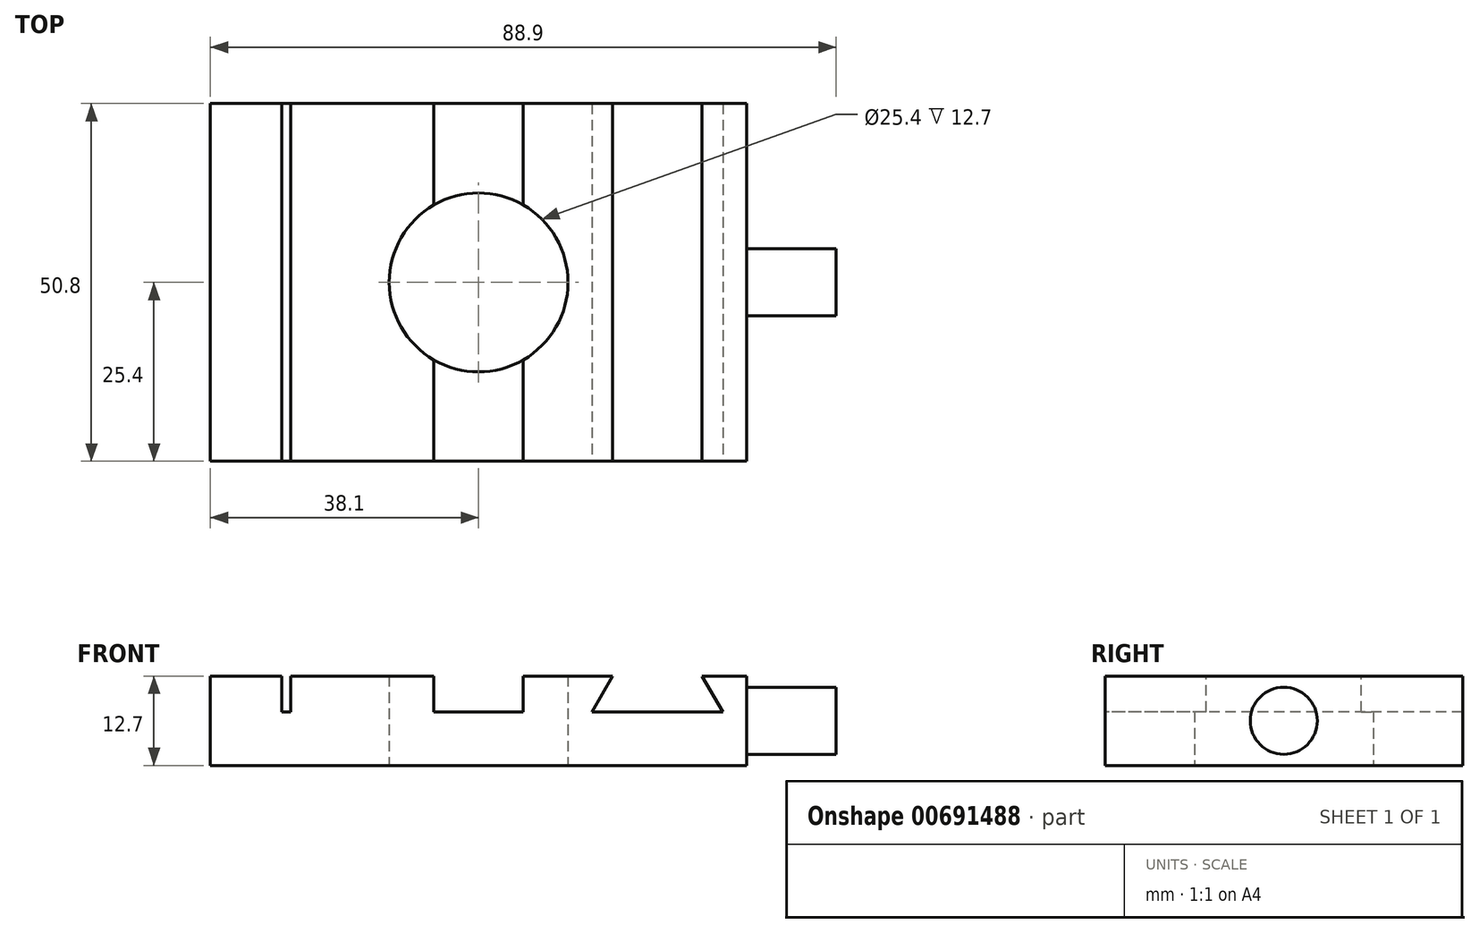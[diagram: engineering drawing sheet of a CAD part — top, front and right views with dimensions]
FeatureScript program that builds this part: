
annotation { "Feature Type Name" : "Feature", "Feature Type Description" : "" }
export const myFeature = defineFeature(function(context is Context, id is Id, definition is map)
    precondition{}
    {
        {
            var Q0;
            Q0=qCreatedBy(makeId("Top.planeOp"),FACE);
            var sketch = newSketch(context, id + "F0", { "sketchPlane" : qUnion([Q0])});
            skLineSegment(sketch, "E0.bottom", {"start": v(38.1, 25.4) * mm, "end": v(-38.1, 25.4) * mm});
            skLineSegment(sketch, "E0.top", {"start": v(38.1, -25.4) * mm, "end": v(-38.1, -25.4) * mm});
            skLineSegment(sketch, "E0.left", {"start": v(38.1, 25.4) * mm, "end": v(38.1, -25.4) * mm});
            skLineSegment(sketch, "E0.right", {"start": v(-38.1, 25.4) * mm, "end": v(-38.1, -25.4) * mm});
            skPoint(sketch, "E0.middle", {"position": v(0, 0) * mm});
            skCircle(sketch, "E1", {"center": v(0, 0) * mm, "radius": 12.7 * mm});
            skSolve(sketch);
        }
        {
            var Q0;
            Q0=makeQuery(id+"F0.imprint","IMPRINT",FACE,{"disambiguationData":[TD([[makeQuery(id+"F0.imprint","IMPRINT",EDGE,{"derivedFrom":sQuery(id+"F0.wireOp",EDGE,"E0.bottom")}),1.0]])]});
            extrude(context, id + "F1", {"entities" : qUnion([Q0]), "depth" : 12.7 * mm, "offsetDistance" : 25 * mm});
        }
        {
            var Q0;
            Q0=makeQuery(id+"F1.opExtrude","CAP_FACE",FACE,{"disambiguationData":[OSD([sQuery(id+"F0.wireOp",EDGE,"E0.bottom"),sQuery(id+"F0.wireOp",EDGE,"E0.top"),sQuery(id+"F0.wireOp",EDGE,"E0.left"),sQuery(id+"F0.wireOp",EDGE,"E0.right"),sQuery(id+"F0.wireOp",EDGE,"E1")])],"isStart":false});
            var sketch = newSketch(context, id + "F2", { "sketchPlane" : qUnion([Q0])});
            skLineSegment(sketch, "E2.bottom", {"start": v(-27.94, 25.4) * mm, "end": v(-26.67, 25.4) * mm});
            skLineSegment(sketch, "E2.top", {"start": v(-27.94, -25.4) * mm, "end": v(-26.67, -25.4) * mm});
            skLineSegment(sketch, "E2.left", {"start": v(-27.94, 25.4) * mm, "end": v(-27.94, -25.4) * mm});
            skLineSegment(sketch, "E2.right", {"start": v(-26.67, 25.4) * mm, "end": v(-26.67, -25.4) * mm});
            skLineSegment(sketch, "E3", {"start": v(-6.35, 25.4) * mm, "end": v(-6.35, -25.4) * mm});
            skLineSegment(sketch, "E4", {"start": v(-6.35, -25.4) * mm, "end": v(6.35, -25.4) * mm});
            skLineSegment(sketch, "E5", {"start": v(6.35, -25.4) * mm, "end": v(6.35, 25.4) * mm});
            skPoint(sketch, "E6", {"position": v(0, 0) * mm});
            skLineSegment(sketch, "E7", {"start": v(0, -25.4) * mm, "end": v(0, 25.4) * mm, "construction": true});
            skSolve(sketch);
        }
        {
            var Q0;
            Q0=makeQuery(id+"F2.imprint","IMPRINT",FACE,{"disambiguationData":[TD([[makeQuery(id+"F2.imprint","IMPRINT",EDGE,{"derivedFrom":sQuery(id+"F2.wireOp",EDGE,"E2.bottom")}),1.0]])]});
            var Q1;
            {var subQ0=sQuery(id+"F2.wireOp",EDGE,"E3");var subQ1=makeQuery(id+"F1.opExtrude","CAP_EDGE",EDGE,{"disambiguationData":[OSD([sQuery(id+"F0.wireOp",EDGE,"E0.bottom")])],"isStart":false});var subQ2=makeQuery(id+"F2.imprint","INTERSECT",VERTEX,{"derivedFrom":[subQ1,subQ0]});Q1=makeQuery(id+"F2.imprint","IMPRINT",FACE,{"disambiguationData":[TD([[makeQuery(id+"F2.imprint","IMPRINT",EDGE,{"disambiguationData":[TD([[subQ2,-1.0]])],"derivedFrom":subQ0}),1.0]])]});}
            var Q2;
            {var subQ0=sQuery(id+"F2.wireOp",EDGE,"E4");Q2=makeQuery(id+"F2.imprint","IMPRINT",FACE,{"disambiguationData":[TD([[makeQuery(id+"F2.imprint","IMPRINT",EDGE,{"derivedFrom":subQ0}),-1.0]])]});}
            extrude(context, id + "F3", {"entities" : qUnion([Q0, Q1, Q2]), "operationType" : NewBodyOperationType.REMOVE, "oppositeDirection" : true, "depth" : 5.08 * mm, "offsetDistance" : 25.4 * mm});
        }
        {
            var Q0;
            Q0=makeQuery(id+"F1.opExtrude","SWEPT_FACE",FACE,{"disambiguationData":[OSD([sQuery(id+"F0.wireOp",EDGE,"E0.top")])]});
            var sketch = newSketch(context, id + "F4", { "sketchPlane" : qUnion([Q0])});
            skLineSegment(sketch, "E8", {"start": v(19.05, 12.7) * mm, "end": v(16.12, 7.62) * mm});
            skLineSegment(sketch, "E9", {"start": v(16.12, 7.62) * mm, "end": v(34.68, 7.62) * mm});
            skLineSegment(sketch, "E10", {"start": v(34.68, 7.62) * mm, "end": v(31.75, 12.7) * mm});
            skLineSegment(sketch, "E11", {"start": v(31.75, 12.7) * mm, "end": v(19.05, 12.7) * mm});
            skLineSegment(sketch, "E12", {"start": v(25.4, 7.62) * mm, "end": v(25.4, 12.7) * mm, "construction": true});
            skSolve(sketch);
        }
        {
            var Q0;
            Q0=makeQuery(id+"F4.imprint","IMPRINT",FACE,{"disambiguationData":[TD([[makeQuery(id+"F4.imprint","IMPRINT",EDGE,{"derivedFrom":sQuery(id+"F4.wireOp",EDGE,"E8")}),1.0]])]});
            extrude(context, id + "F5", {"entities" : qUnion([Q0]), "operationType" : NewBodyOperationType.REMOVE, "endBound" : BoundingType.UP_TO_NEXT, "oppositeDirection" : true, "depth" : 25.4 * mm, "offsetDistance" : 25.4 * mm});
        }
        {
            var Q0;
            Q0=makeQuery(id+"F1.opExtrude","SWEPT_FACE",FACE,{"disambiguationData":[OSD([sQuery(id+"F0.wireOp",EDGE,"E0.left")])]});
            var sketch = newSketch(context, id + "F6", { "sketchPlane" : qUnion([Q0])});
            skCircle(sketch, "E13", {"center": v(0, 6.35) * mm, "radius": 4.76 * mm});
            skPoint(sketch, "E13.centerSnap0", {"position": v(-25.4, 6.35) * mm});
            skPoint(sketch, "E13.centerSnap1", {"position": v(0, 12.7) * mm});
            skSolve(sketch);
        }
        {
            var Q0;
            Q0=makeQuery(id+"F6.imprint","IMPRINT",FACE,{"disambiguationData":[TD([[makeQuery(id+"F6.imprint","IMPRINT",EDGE,{"derivedFrom":sQuery(id+"F6.wireOp",EDGE,"E13")}),1.0]])]});
            extrude(context, id + "F7", {"entities" : qUnion([Q0]), "operationType" : NewBodyOperationType.ADD, "depth" : 12.7 * mm, "offsetDistance" : 25.4 * mm});
        }
    });
